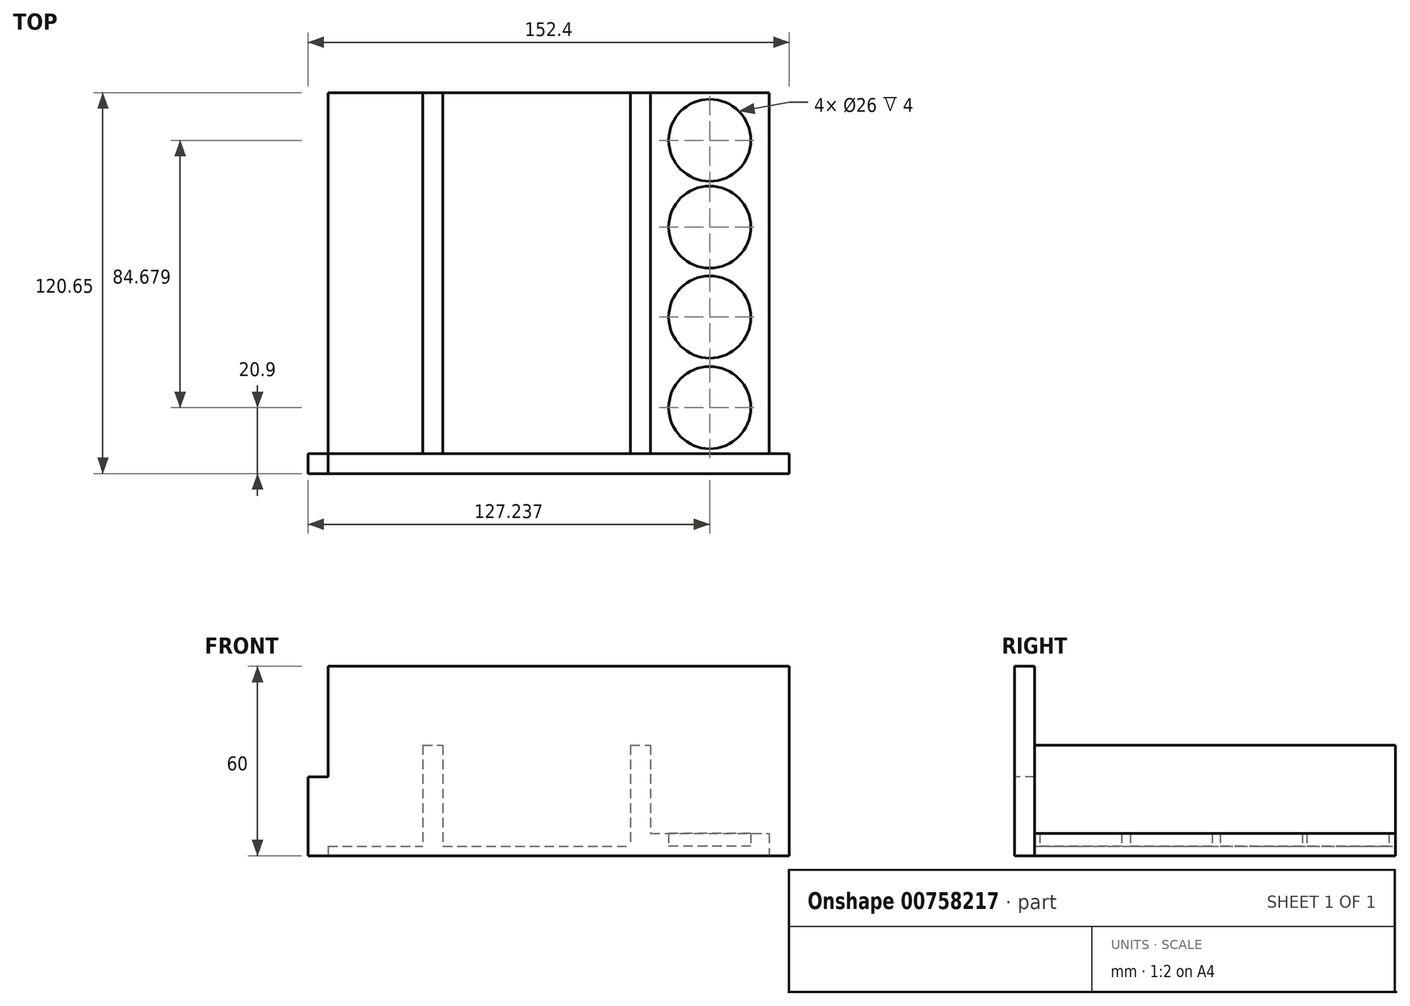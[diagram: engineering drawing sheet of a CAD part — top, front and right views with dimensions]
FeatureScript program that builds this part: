
annotation { "Feature Type Name" : "Feature", "Feature Type Description" : "" }
export const myFeature = defineFeature(function(context is Context, id is Id, definition is map)
    precondition{}
    {
        {
            var Q0;
            Q0=qCreatedBy(makeId("Top.planeOp"),FACE);
            var sketch = newSketch(context, id + "F0", { "sketchPlane" : qUnion([Q0])});
            skLineSegment(sketch, "E0.bottom", {"start": v(-76.2, 63.5) * mm, "end": v(76.2, 63.5) * mm});
            skLineSegment(sketch, "E0.top", {"start": v(-76.2, -63.5) * mm, "end": v(76.2, -63.5) * mm});
            skLineSegment(sketch, "E0.left", {"start": v(-76.2, 63.5) * mm, "end": v(-76.2, -63.5) * mm});
            skLineSegment(sketch, "E0.right", {"start": v(76.2, 63.5) * mm, "end": v(76.2, -63.5) * mm});
            skPoint(sketch, "E0.middle", {"position": v(0, 0) * mm});
            skLineSegment(sketch, "E1.0", {"start": v(-69.85, 63.5) * mm, "end": v(-69.85, -63.5) * mm});
            skLineSegment(sketch, "E2.0", {"start": v(-76.2, 57.15) * mm, "end": v(76.2, 57.15) * mm});
            skLineSegment(sketch, "E3.0", {"start": v(-76.2, -57.15) * mm, "end": v(76.2, -57.15) * mm});
            skLineSegment(sketch, "E4.0", {"start": v(69.85, 63.5) * mm, "end": v(69.85, -63.5) * mm});
            skLineSegment(sketch, "E5", {"start": v(-39.86, -57.15) * mm, "end": v(-39.86, 57.15) * mm});
            skLineSegment(sketch, "E6", {"start": v(25.87, 57.15) * mm, "end": v(25.87, -57.15) * mm});
            skLineSegment(sketch, "E7.0", {"start": v(-33.51, -57.15) * mm, "end": v(-33.51, 57.15) * mm});
            skLineSegment(sketch, "E8.0", {"start": v(32.22, 57.15) * mm, "end": v(32.22, -57.15) * mm});
            skCircle(sketch, "E9", {"center": v(51.04, 42.08) * mm, "radius": 13 * mm});
            skCircle(sketch, "E10", {"center": v(51.04, 14.6) * mm, "radius": 13 * mm});
            skCircle(sketch, "E11", {"center": v(51.04, -13.9) * mm, "radius": 13 * mm});
            skCircle(sketch, "E12", {"center": v(51.04, -42.6) * mm, "radius": 13 * mm});
            skLineSegment(sketch, "E13", {"start": v(32.22, 57.15) * mm, "end": v(69.85, 57.15) * mm});
            skLineSegment(sketch, "E14", {"start": v(69.85, 57.15) * mm, "end": v(76.2, 57.15) * mm});
            skLineSegment(sketch, "E15", {"start": v(-76.2, 57.15) * mm, "end": v(-69.85, 57.15) * mm});
            skLineSegment(sketch, "E16", {"start": v(-69.85, 57.15) * mm, "end": v(-39.86, 57.15) * mm});
            skLineSegment(sketch, "E17", {"start": v(-33.51, 57.15) * mm, "end": v(25.87, 57.15) * mm});
            skLineSegment(sketch, "E18", {"start": v(51.04, 57.15) * mm, "end": v(51.04, -57.15) * mm});
            skSolve(sketch);
        }
        {
            var Q0;
            {var subQ0=sQuery(id+"F0.wireOp",EDGE,"E0.left");var subQ1=sQuery(id+"F0.wireOp",EDGE,"E0.top");var subQ2=makeQuery(id+"F0.imprint","INTERSECT",VERTEX,{"derivedFrom":[subQ1,subQ0]});Q0=makeQuery(id+"F0.imprint","IMPRINT",FACE,{"disambiguationData":[TD([[makeQuery(id+"F0.imprint","IMPRINT",EDGE,{"disambiguationData":[TD([[subQ2,-1.0]])],"derivedFrom":subQ1}),1.0]])]});}
            var Q1;
            {var subQ3=sQuery(id+"F0.wireOp",EDGE,"E15");Q1=makeQuery(id+"F0.imprint","IMPRINT",FACE,{"disambiguationData":[TD([[makeQuery(id+"F0.imprint","IMPRINT",EDGE,{"derivedFrom":subQ3}),-1.0]])]});}
            var Q2;
            {var subQ5=sQuery(id+"F0.wireOp",EDGE,"E15");Q2=makeQuery(id+"F0.imprint","IMPRINT",FACE,{"disambiguationData":[TD([[makeQuery(id+"F0.imprint","IMPRINT",EDGE,{"derivedFrom":subQ5}),1.0]])]});}
            extrude(context, id + "F1", {"entities" : qUnion([Q0, Q1, Q2]), "depth" : 25 * mm, "offsetDistance" : 25 * mm});
        }
        {
            var Q0;
            {var subQ2=sQuery(id+"F0.wireOp",EDGE,"E1.0");var subQ5=sQuery(id+"F0.wireOp",EDGE,"E0.top");var subQ6=makeQuery(id+"F0.imprint","INTERSECT",VERTEX,{"derivedFrom":[subQ5,subQ2]});Q0=makeQuery(id+"F0.imprint","IMPRINT",FACE,{"disambiguationData":[TD([[makeQuery(id+"F0.imprint","IMPRINT",EDGE,{"disambiguationData":[TD([[subQ6,-1.0]])],"derivedFrom":subQ5}),1.0]])]});}
            var Q1;
            {var subQ0=sQuery(id+"F0.wireOp",EDGE,"E16");Q1=makeQuery(id+"F0.imprint","IMPRINT",FACE,{"disambiguationData":[TD([[makeQuery(id+"F0.imprint","IMPRINT",EDGE,{"derivedFrom":subQ0}),1.0]])]});}
            var Q2;
            {var subQ3=sQuery(id+"F0.wireOp",EDGE,"E14");Q2=makeQuery(id+"F0.imprint","IMPRINT",FACE,{"disambiguationData":[TD([[makeQuery(id+"F0.imprint","IMPRINT",EDGE,{"derivedFrom":subQ3}),-1.0]])]});}
            var Q3;
            {var subQ0=sQuery(id+"F0.wireOp",EDGE,"E0.right");var subQ1=sQuery(id+"F0.wireOp",EDGE,"E0.top");var subQ2=makeQuery(id+"F0.imprint","INTERSECT",VERTEX,{"derivedFrom":[subQ1,subQ0]});Q3=makeQuery(id+"F0.imprint","IMPRINT",FACE,{"disambiguationData":[TD([[makeQuery(id+"F0.imprint","IMPRINT",EDGE,{"disambiguationData":[TD([[subQ2,1.0]])],"derivedFrom":subQ1}),1.0]])]});}
            var Q4;
            {var subQ5=sQuery(id+"F0.wireOp",EDGE,"E14");Q4=makeQuery(id+"F0.imprint","IMPRINT",FACE,{"disambiguationData":[TD([[makeQuery(id+"F0.imprint","IMPRINT",EDGE,{"derivedFrom":subQ5}),1.0]])]});}
            extrude(context, id + "F2", {"entities" : qUnion([Q0, Q1, Q2, Q3, Q4]), "operationType" : NewBodyOperationType.ADD, "depth" : 60 * mm, "offsetDistance" : 25 * mm});
        }
        {
            var Q0;
            {var subQ0=sQuery(id+"F0.wireOp",EDGE,"E5");Q0=makeQuery(id+"F0.imprint","IMPRINT",FACE,{"disambiguationData":[TD([[makeQuery(id+"F0.imprint","IMPRINT",EDGE,{"derivedFrom":subQ0}),-1.0]])]});}
            var Q1;
            {var subQ2=sQuery(id+"F0.wireOp",EDGE,"E6");Q1=makeQuery(id+"F0.imprint","IMPRINT",FACE,{"disambiguationData":[TD([[makeQuery(id+"F0.imprint","IMPRINT",EDGE,{"derivedFrom":subQ2}),1.0]])]});}
            extrude(context, id + "F3", {"entities" : qUnion([Q0, Q1]), "operationType" : NewBodyOperationType.ADD, "depth" : 35 * mm, "offsetDistance" : 25 * mm});
        }
        {
            var Q0;
            {var subQ15=sQuery(id+"F0.wireOp",EDGE,"E8.0");Q0=makeQuery(id+"F0.imprint","IMPRINT",FACE,{"disambiguationData":[TD([[makeQuery(id+"F0.imprint","IMPRINT",EDGE,{"derivedFrom":subQ15}),1.0]])]});}
            var Q1;
            {var subQ0=sQuery(id+"F0.wireOp",EDGE,"E18");var subQ12=sQuery(id+"F0.wireOp",EDGE,"E3.0");var subQ13=makeQuery(id+"F0.imprint","INTERSECT",VERTEX,{"derivedFrom":[subQ12,subQ0]});Q1=makeQuery(id+"F0.imprint","IMPRINT",FACE,{"disambiguationData":[TD([[makeQuery(id+"F0.imprint","IMPRINT",EDGE,{"disambiguationData":[TD([[subQ13,-1.0]])],"derivedFrom":subQ12}),1.0]])]});}
            extrude(context, id + "F4", {"entities" : qUnion([Q0, Q1]), "operationType" : NewBodyOperationType.ADD, "depth" : 7 * mm, "offsetDistance" : 25 * mm});
        }
        {
            var Q0;
            {var subQ4=sQuery(id+"F0.wireOp",EDGE,"E5");Q0=makeQuery(id+"F0.imprint","IMPRINT",FACE,{"disambiguationData":[TD([[makeQuery(id+"F0.imprint","IMPRINT",EDGE,{"derivedFrom":subQ4}),1.0]])]});}
            var Q1;
            {var subQ0=sQuery(id+"F0.wireOp",EDGE,"E6");Q1=makeQuery(id+"F0.imprint","IMPRINT",FACE,{"disambiguationData":[TD([[makeQuery(id+"F0.imprint","IMPRINT",EDGE,{"derivedFrom":subQ0}),-1.0]])]});}
            var Q2;
            {var subQ0=sQuery(id+"F0.wireOp",EDGE,"E18");var subQ1=sQuery(id+"F0.wireOp",EDGE,"E12");var subQ2=makeQuery(id+"F0.imprint","INTERSECT",VERTEX,{"disambiguationData":[OD(0.0)],"derivedFrom":[subQ1,subQ0]});Q2=makeQuery(id+"F0.imprint","IMPRINT",FACE,{"disambiguationData":[TD([[makeQuery(id+"F0.imprint","IMPRINT",EDGE,{"disambiguationData":[TD([[subQ2,-1.0]])],"derivedFrom":subQ1}),1.0]])]});}
            var Q3;
            {var subQ0=sQuery(id+"F0.wireOp",EDGE,"E18");var subQ1=sQuery(id+"F0.wireOp",EDGE,"E12");var subQ2=makeQuery(id+"F0.imprint","INTERSECT",VERTEX,{"disambiguationData":[OD(0.0)],"derivedFrom":[subQ1,subQ0]});Q3=makeQuery(id+"F0.imprint","IMPRINT",FACE,{"disambiguationData":[TD([[makeQuery(id+"F0.imprint","IMPRINT",EDGE,{"disambiguationData":[TD([[subQ2,1.0]])],"derivedFrom":subQ1}),1.0]])]});}
            var Q4;
            {var subQ0=sQuery(id+"F0.wireOp",EDGE,"E18");var subQ1=sQuery(id+"F0.wireOp",EDGE,"E11");var subQ2=makeQuery(id+"F0.imprint","INTERSECT",VERTEX,{"disambiguationData":[OD(0.0)],"derivedFrom":[subQ1,subQ0]});Q4=makeQuery(id+"F0.imprint","IMPRINT",FACE,{"disambiguationData":[TD([[makeQuery(id+"F0.imprint","IMPRINT",EDGE,{"disambiguationData":[TD([[subQ2,1.0]])],"derivedFrom":subQ1}),1.0]])]});}
            var Q5;
            {var subQ0=sQuery(id+"F0.wireOp",EDGE,"E18");var subQ1=sQuery(id+"F0.wireOp",EDGE,"E11");var subQ2=makeQuery(id+"F0.imprint","INTERSECT",VERTEX,{"disambiguationData":[OD(0.0)],"derivedFrom":[subQ1,subQ0]});Q5=makeQuery(id+"F0.imprint","IMPRINT",FACE,{"disambiguationData":[TD([[makeQuery(id+"F0.imprint","IMPRINT",EDGE,{"disambiguationData":[TD([[subQ2,-1.0]])],"derivedFrom":subQ1}),1.0]])]});}
            var Q6;
            {var subQ0=sQuery(id+"F0.wireOp",EDGE,"E18");var subQ1=sQuery(id+"F0.wireOp",EDGE,"E10");var subQ2=makeQuery(id+"F0.imprint","INTERSECT",VERTEX,{"disambiguationData":[OD(0.0)],"derivedFrom":[subQ1,subQ0]});Q6=makeQuery(id+"F0.imprint","IMPRINT",FACE,{"disambiguationData":[TD([[makeQuery(id+"F0.imprint","IMPRINT",EDGE,{"disambiguationData":[TD([[subQ2,-1.0]])],"derivedFrom":subQ1}),1.0]])]});}
            var Q7;
            {var subQ0=sQuery(id+"F0.wireOp",EDGE,"E18");var subQ1=sQuery(id+"F0.wireOp",EDGE,"E10");var subQ2=makeQuery(id+"F0.imprint","INTERSECT",VERTEX,{"disambiguationData":[OD(0.0)],"derivedFrom":[subQ1,subQ0]});Q7=makeQuery(id+"F0.imprint","IMPRINT",FACE,{"disambiguationData":[TD([[makeQuery(id+"F0.imprint","IMPRINT",EDGE,{"disambiguationData":[TD([[subQ2,1.0]])],"derivedFrom":subQ1}),1.0]])]});}
            var Q8;
            {var subQ0=sQuery(id+"F0.wireOp",EDGE,"E18");var subQ1=sQuery(id+"F0.wireOp",EDGE,"E9");var subQ2=makeQuery(id+"F0.imprint","INTERSECT",VERTEX,{"disambiguationData":[OD(0.0)],"derivedFrom":[subQ1,subQ0]});Q8=makeQuery(id+"F0.imprint","IMPRINT",FACE,{"disambiguationData":[TD([[makeQuery(id+"F0.imprint","IMPRINT",EDGE,{"disambiguationData":[TD([[subQ2,1.0]])],"derivedFrom":subQ1}),1.0]])]});}
            var Q9;
            {var subQ0=sQuery(id+"F0.wireOp",EDGE,"E18");var subQ1=sQuery(id+"F0.wireOp",EDGE,"E9");var subQ2=makeQuery(id+"F0.imprint","INTERSECT",VERTEX,{"disambiguationData":[OD(0.0)],"derivedFrom":[subQ1,subQ0]});Q9=makeQuery(id+"F0.imprint","IMPRINT",FACE,{"disambiguationData":[TD([[makeQuery(id+"F0.imprint","IMPRINT",EDGE,{"disambiguationData":[TD([[subQ2,-1.0]])],"derivedFrom":subQ1}),1.0]])]});}
            extrude(context, id + "F5", {"entities" : qUnion([Q0, Q1, Q2, Q3, Q4, Q5, Q6, Q7, Q8, Q9]), "operationType" : NewBodyOperationType.ADD, "depth" : 3 * mm, "offsetDistance" : 25 * mm});
        }
    });
